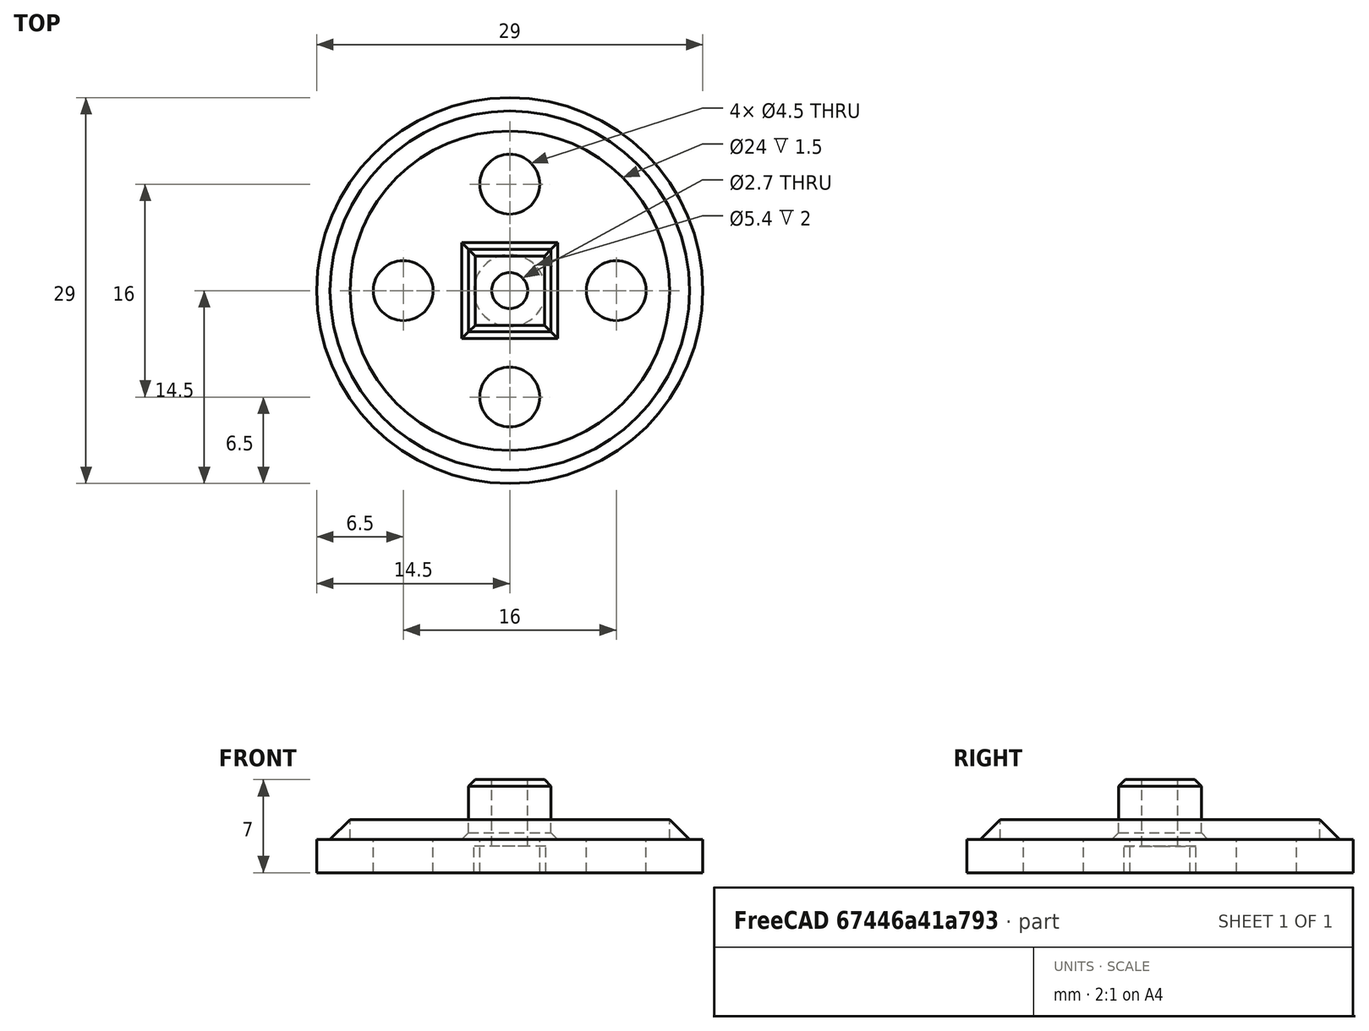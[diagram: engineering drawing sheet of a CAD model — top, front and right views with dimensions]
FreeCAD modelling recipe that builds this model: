
FCSTD DOCUMENT  (FreeCAD 0.15R4671 (Git))
Label: tendon_wheel_ax_18_top_3_mm
License: CC-BY 3.0
LicenseURL: http://creativecommons.org/licenses/by/3.0/
objects: Part::Cylinder×8, Part::MultiFuse×4, Part::Cut×3, Part::Chamfer×2, Part::Cone×1, Part::Box×1
note: 19 computed .brp shape members not serialized (recipe doc carries the construction recipe); baked Part::Feature solids carry a one-line shape summary decoded from their .brp

FEATURE [Part::Cylinder] Cylinder
  Angle = 360
  Height = 6
  Placement = pos=(0,0,2) rot=(0,0,1;0rad)
  Radius = 12
FEATURE [Part::Cylinder] Cylinder001
  Angle = 360
  Height = 2.5
  Placement = pos=(0,0,-0.5) rot=(0,0,1;0rad)
  Radius = 14.5
FEATURE [Part::Cone] Cone
  Angle = 360
  Height = 3.5
  Placement = pos=(0,0,1) rot=(0,0,1;0rad)
  Radius1 = 14.5
  Radius2 = 11
FEATURE [Part::Box] Box  label="Cube"
  Height = 4.5
  Length = 6.2
  Placement = pos=(-3.1,-3.1,2) rot=(0,0,1;0rad)
  Width = 6.2
FEATURE [Part::MultiFuse] Fusion
  Shapes = -> [Cone,Cylinder001]
FEATURE [Part::Cylinder] Cylinder002  label="Cylinder004"
  Angle = 360
  Height = 20
  Placement = pos=(0,0,-5) rot=(0,0,1;0rad)
  Radius = 1.35
FEATURE [Part::Cut] Cut
  Base = -> Fusion
  Tool = -> Cylinder
FEATURE [Part::MultiFuse] Fusion001
  Shapes = -> [Cut,Box]
FEATURE [Part::Cylinder] Cylinder003  label="Cylinder012"
  Angle = 360
  Height = 2
  Placement = pos=(0,0,-0.5) rot=(0,0,1;0rad)
  Radius = 2.7
FEATURE [Part::MultiFuse] Fusion002
  Shapes = -> [Cylinder003,Cylinder002]
FEATURE [Part::Cut] Cut001
  Base = -> Fusion001
  Tool = -> Fusion002
FEATURE [Part::Chamfer] Chamfer
  Base = -> Cut001
  Edges = 4 edges r=0.5: [Edge1,Edge2,Edge3,Edge4]
FEATURE [Part::Cylinder] Cylinder005  label="TopHole005"
  Angle = 360
  Height = 20
  Placement = pos=(8,0,-4) rot=(0,0,1;0rad)
  Radius = 2.25
FEATURE [Part::Cylinder] Cylinder008  label="TopHole006"
  Angle = 360
  Height = 20
  Placement = pos=(0,8,-4) rot=(0,0,1;0rad)
  Radius = 2.25
FEATURE [Part::Cylinder] Cylinder009  label="TopHole004"
  Angle = 360
  Height = 20
  Placement = pos=(-8,0,-4) rot=(0,0,1;0rad)
  Radius = 2.25
FEATURE [Part::Cylinder] Cylinder011  label="TopHole007"
  Angle = 360
  Height = 20
  Placement = pos=(0,-8,-4) rot=(0,0,1;0rad)
  Radius = 2.25
FEATURE [Part::MultiFuse] Fusion003
  Shapes = -> [Cylinder011,Cylinder008,Cylinder009,Cylinder005]
FEATURE [Part::Cut] Cut002
  Base = -> Chamfer
  Tool = -> Fusion003
FEATURE [Part::Chamfer] Chamfer001
  Base = -> Cut002
  Edges = 4 edges r=0.5: [Edge17,Edge20,Edge22,Edge23]
